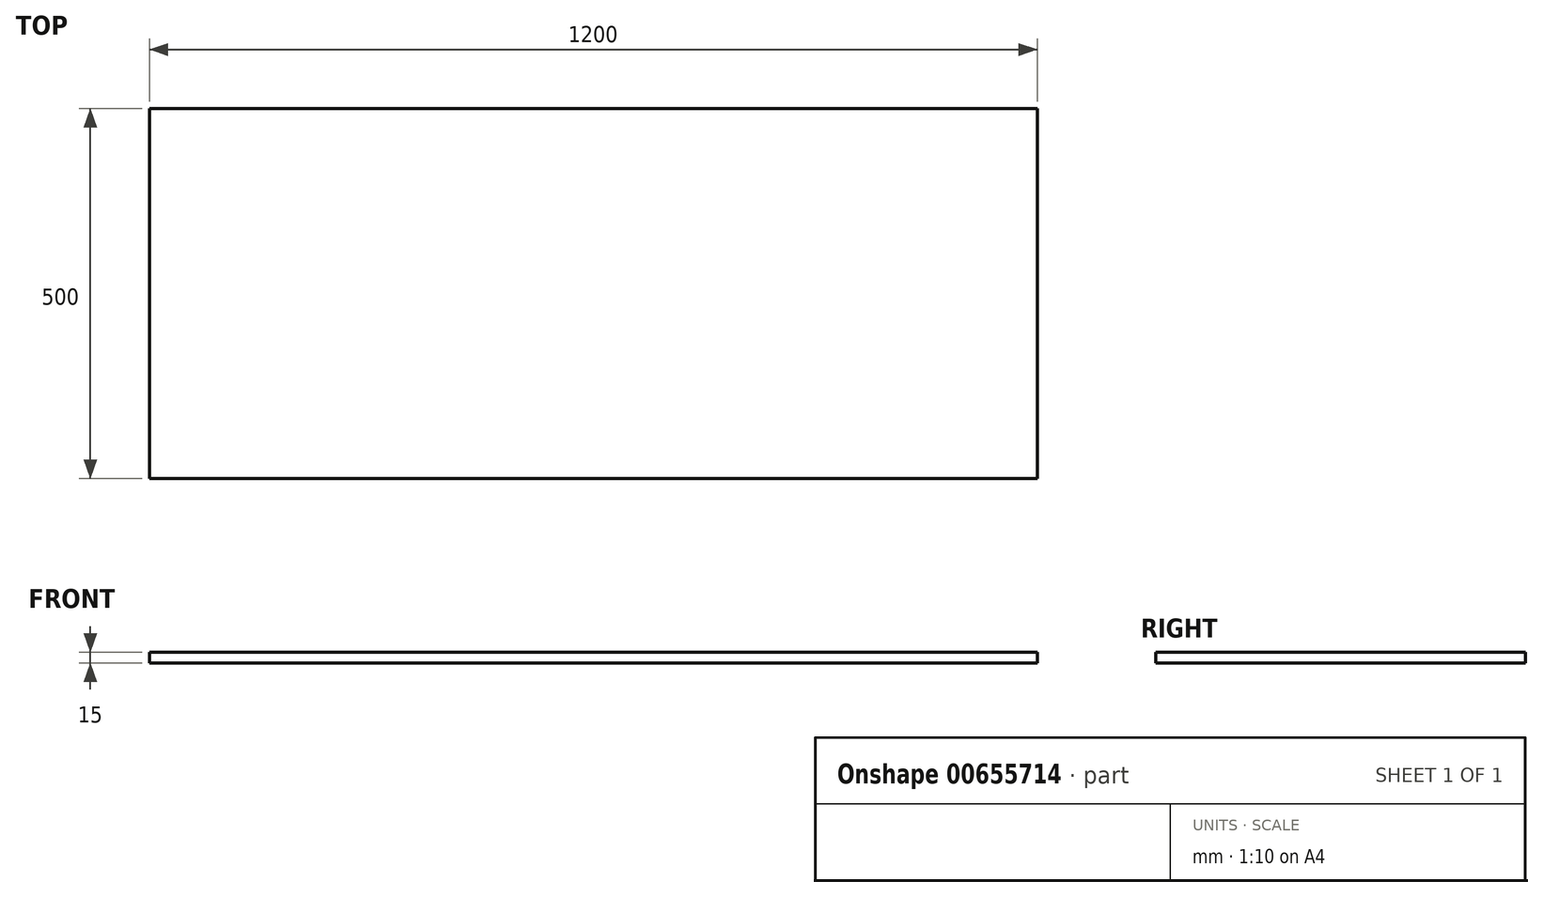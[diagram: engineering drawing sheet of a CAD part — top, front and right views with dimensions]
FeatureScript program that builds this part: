
annotation { "Feature Type Name" : "Feature", "Feature Type Description" : "" }
export const myFeature = defineFeature(function(context is Context, id is Id, definition is map)
    precondition{}
    {
        {
            var Q0;
            Q0=qCreatedBy(makeId("Top.planeOp"),FACE);
            var sketch = newSketch(context, id + "F0", { "sketchPlane" : qUnion([Q0])});
            skLineSegment(sketch, "E0.bottom", {"start": v(-1200, 500) * mm, "end": v(0, 500) * mm});
            skLineSegment(sketch, "E0.top", {"start": v(-1200, 0) * mm, "end": v(0, 0) * mm});
            skLineSegment(sketch, "E0.left", {"start": v(-1200, 500) * mm, "end": v(-1200, 0) * mm});
            skLineSegment(sketch, "E0.right", {"start": v(0, 500) * mm, "end": v(0, 0) * mm});
            skSolve(sketch);
        }
        {
            var Q0;
            Q0=makeQuery(id+"F0.imprint","IMPRINT",FACE,{"disambiguationData":[TD([[makeQuery(id+"F0.imprint","IMPRINT",EDGE,{"derivedFrom":sQuery(id+"F0.wireOp",EDGE,"E0.bottom")}),-1.0]])]});
            extrude(context, id + "F1", {"entities" : qUnion([Q0]), "depth" : 15 * mm, "offsetDistance" : 25 * mm});
        }
    });
